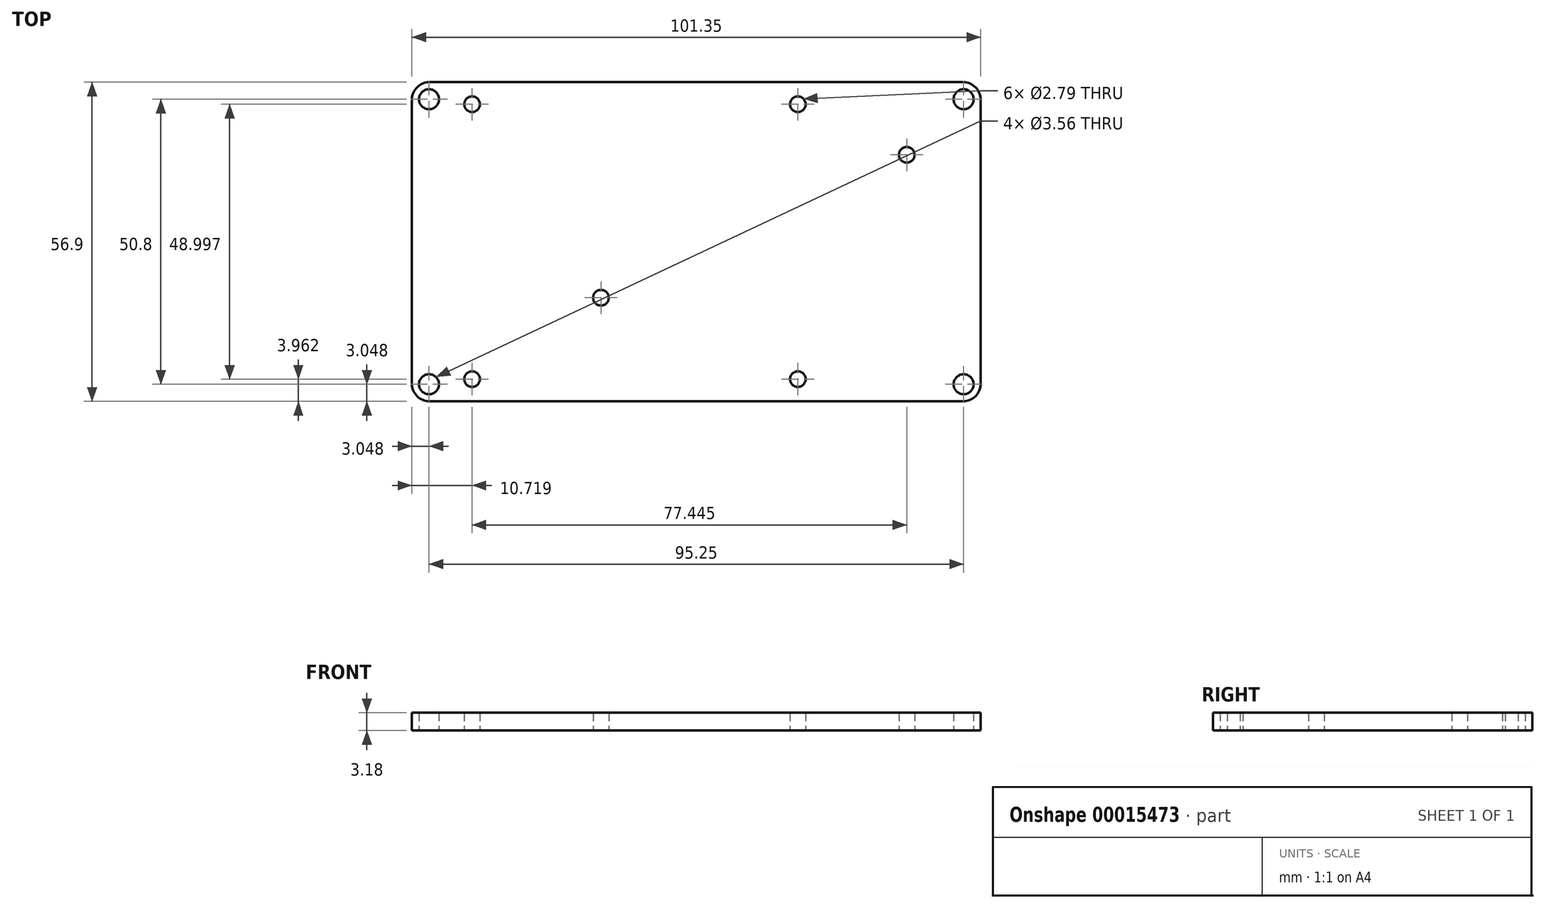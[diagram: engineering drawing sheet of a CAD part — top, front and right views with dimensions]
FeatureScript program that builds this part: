
annotation { "Feature Type Name" : "Feature", "Feature Type Description" : "" }
export const myFeature = defineFeature(function(context is Context, id is Id, definition is map)
    precondition{}
    {
        {
            var Q0;
            Q0=qCreatedBy(makeId("Top.planeOp"),FACE);
            var sketch = newSketch(context, id + "F0", { "sketchPlane" : qUnion([Q0])});
            skLineSegment(sketch, "E0.bottom", {"start": v(3.17, 0) * mm, "end": v(98.17, 0) * mm});
            skLineSegment(sketch, "E0.top", {"start": v(3.17, 56.9) * mm, "end": v(98.17, 56.9) * mm});
            skLineSegment(sketch, "E0.left", {"start": v(0, 3.18) * mm, "end": v(0, 53.72) * mm});
            skLineSegment(sketch, "E0.right", {"start": v(101.35, 3.18) * mm, "end": v(101.35, 53.72) * mm});
            skCircle(sketch, "E1", {"center": v(3.05, 3.05) * mm, "radius": 1.78 * mm});
            skCircle(sketch, "E2", {"center": v(3.05, 53.85) * mm, "radius": 1.78 * mm});
            skCircle(sketch, "E3", {"center": v(98.3, 3.05) * mm, "radius": 1.78 * mm});
            skCircle(sketch, "E4", {"center": v(98.3, 53.85) * mm, "radius": 1.78 * mm});
            skPoint(sketch, "E5.visualSharp", {"position": v(0, 56.9) * mm});
            skArc(sketch, "E5.filletArc", {"start": v(3.17, 56.9) * mm, "mid": v(0.93, 55.97) * mm, "end": v(0, 53.72) * mm});
            skPoint(sketch, "E6.visualSharp", {"position": v(0, 0) * mm});
            skArc(sketch, "E6.filletArc", {"start": v(0, 3.17) * mm, "mid": v(0.93, 0.93) * mm, "end": v(3.17, 0) * mm});
            skPoint(sketch, "E7.visualSharp", {"position": v(101.35, 0) * mm});
            skArc(sketch, "E7.filletArc", {"start": v(98.17, 0) * mm, "mid": v(100.42, 0.93) * mm, "end": v(101.35, 3.18) * mm});
            skPoint(sketch, "E8.visualSharp", {"position": v(101.35, 56.9) * mm});
            skArc(sketch, "E8.filletArc", {"start": v(101.35, 53.72) * mm, "mid": v(100.42, 55.97) * mm, "end": v(98.17, 56.9) * mm});
            skCircle(sketch, "E9", {"center": v(10.72, 3.96) * mm, "radius": 1.4 * mm});
            skCircle(sketch, "E10", {"center": v(33.68, 18.47) * mm, "radius": 1.4 * mm});
            skCircle(sketch, "E11", {"center": v(10.72, 52.96) * mm, "radius": 1.4 * mm});
            skCircle(sketch, "E12", {"center": v(68.76, 52.96) * mm, "radius": 1.4 * mm});
            skCircle(sketch, "E13", {"center": v(88.16, 43.94) * mm, "radius": 1.4 * mm});
            skCircle(sketch, "E14", {"center": v(68.76, 3.96) * mm, "radius": 1.4 * mm});
            skSolve(sketch);
        }
        {
            var Q0;
            Q0 = qSketchRegion(id + "F0", true);
            extrude(context, id + "F1", {"entities" : qUnion([Q0]), "depth" : 3.17 * mm});
        }
    });
